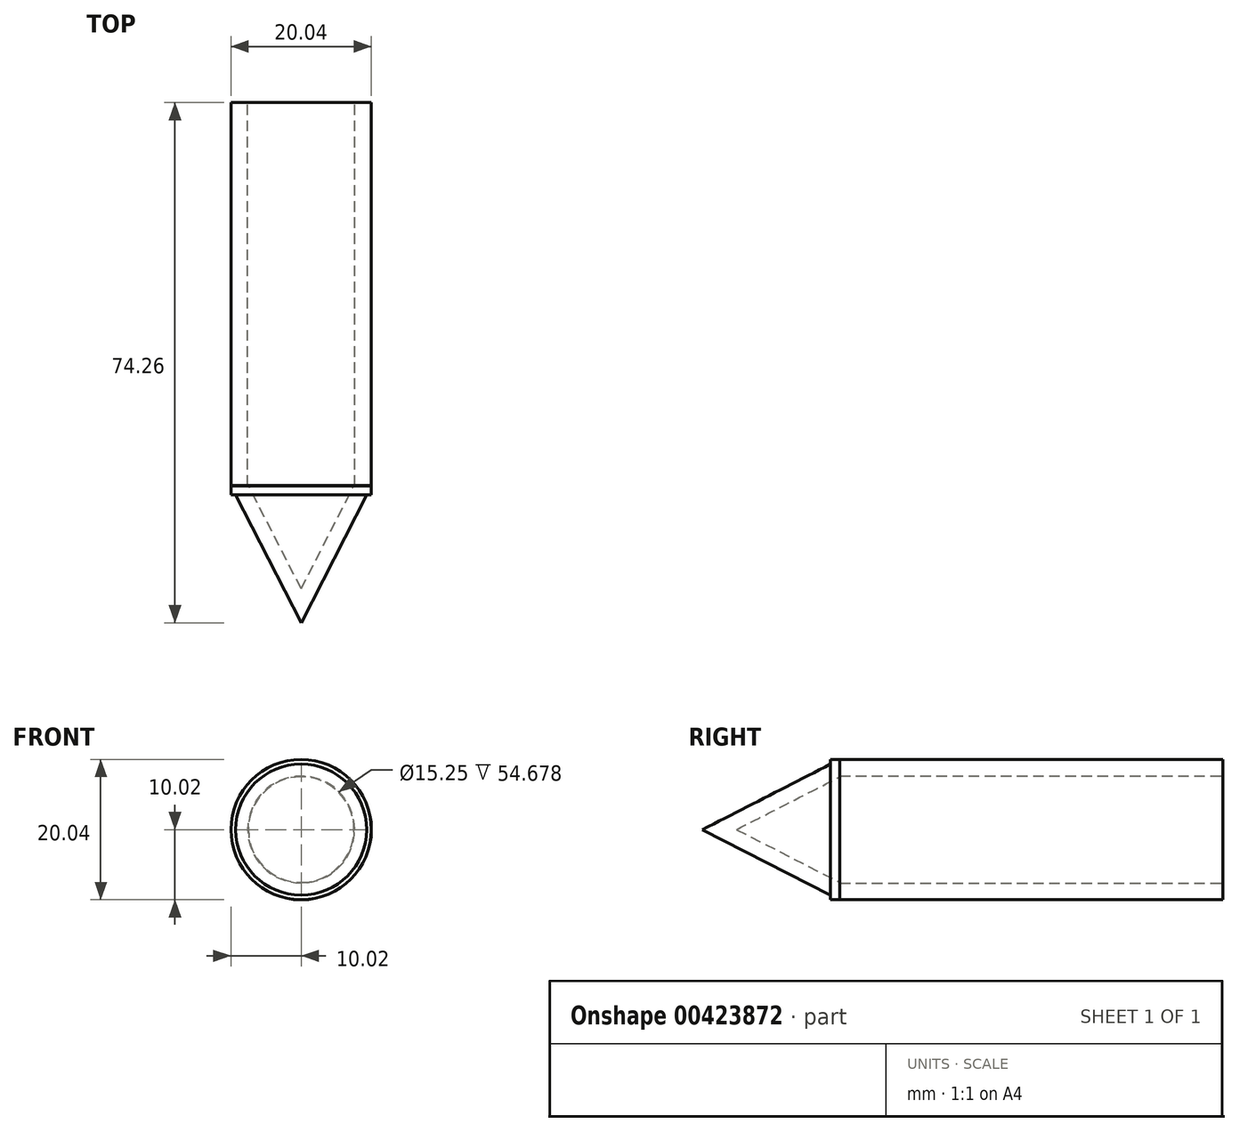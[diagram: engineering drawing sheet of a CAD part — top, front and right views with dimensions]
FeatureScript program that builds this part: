
annotation { "Feature Type Name" : "Feature", "Feature Type Description" : "" }
export const myFeature = defineFeature(function(context is Context, id is Id, definition is map)
    precondition{}
    {
        {
            var Q0;
            Q0=qCreatedBy(makeId("Front.planeOp"),FACE);
            var sketch = newSketch(context, id + "F0", { "sketchPlane" : qUnion([Q0])});
            skCircle(sketch, "E0", {"center": v(0, 0) * mm, "radius": 10.01 * mm});
            skCircle(sketch, "E1", {"center": v(0, 0) * mm, "radius": 7.63 * mm});
            skSolve(sketch);
        }
        {
            var Q0;
            Q0=qCreatedBy(makeId("Front.planeOp"),FACE);
            var sketch = newSketch(context, id + "F1", { "sketchPlane" : qUnion([Q0])});
            skSolve(sketch);
        }
        {
            var Q0;
            Q0 = qSketchRegion(id + "F1", true);
            var Q1;
            Q1=makeQuery(id+"F0.imprint","IMPRINT",FACE,{"disambiguationData":[TD([[makeQuery(id+"F0.imprint","IMPRINT",EDGE,{"derivedFrom":sQuery(id+"F0.wireOp",EDGE,"E0")}),1.0]])]});
            extrude(context, id + "F2", {"entities" : qUnion([Q0, Q1]), "endBound" : BoundingType.SYMMETRIC, "depth" : 50 * mm});
        }
        {
            var Q0;
            Q0=qCreatedBy(makeId("Right.planeOp"),FACE);
            var sketch = newSketch(context, id + "F3", { "sketchPlane" : qUnion([Q0])});
            skLineSegment(sketch, "E2", {"start": v(-23.68, 0) * mm, "end": v(-23.68, -7.53) * mm});
            skLineSegment(sketch, "E3", {"start": v(-23.68, -7.53) * mm, "end": v(-23.68, -10.02) * mm});
            skLineSegment(sketch, "E4", {"start": v(-23.68, -10.02) * mm, "end": v(-43.26, 0) * mm});
            skLineSegment(sketch, "E5", {"start": v(-43.26, 0) * mm, "end": v(-23.68, -10.02) * mm});
            skLineSegment(sketch, "E6", {"start": v(-23.68, -7.53) * mm, "end": v(-38.4, 0) * mm});
            skLineSegment(sketch, "E7", {"start": v(-38.4, 0) * mm, "end": v(-43.26, 0) * mm});
            skLineSegment(sketch, "E8", {"start": v(-38.4, 0) * mm, "end": v(-23.68, 0) * mm});
            skSolve(sketch);
        }
        {
            var Q0;
            Q0=makeQuery(id+"F3.imprint","IMPRINT",FACE,{"disambiguationData":[TD([[makeQuery(id+"F3.imprint","IMPRINT",EDGE,{"derivedFrom":sQuery(id+"F3.wireOp",EDGE,"E3")}),-1.0]])]});
            var Q1;
            Q1=sQuery(id+"F3.wireOp",EDGE,"E8");
            revolve(context, id + "F4", {"operationType" : NewBodyOperationType.ADD, "entities" : qUnion([Q0]), "axis" : qUnion([Q1]), "revolveType" : RevolveType.FULL});
        }
        {
            var Q0;
            Q0=makeQuery(id+"F2.opExtrude","CAP_FACE",FACE,{"disambiguationData":[OSD([sQuery(id+"F0.wireOp",EDGE,"E0"),sQuery(id+"F0.wireOp",EDGE,"E1")])],"isStart":true});
            extrude(context, id + "F5", {"entities" : qUnion([Q0]), "operationType" : NewBodyOperationType.ADD, "depth" : 6 * mm});
        }
    });
